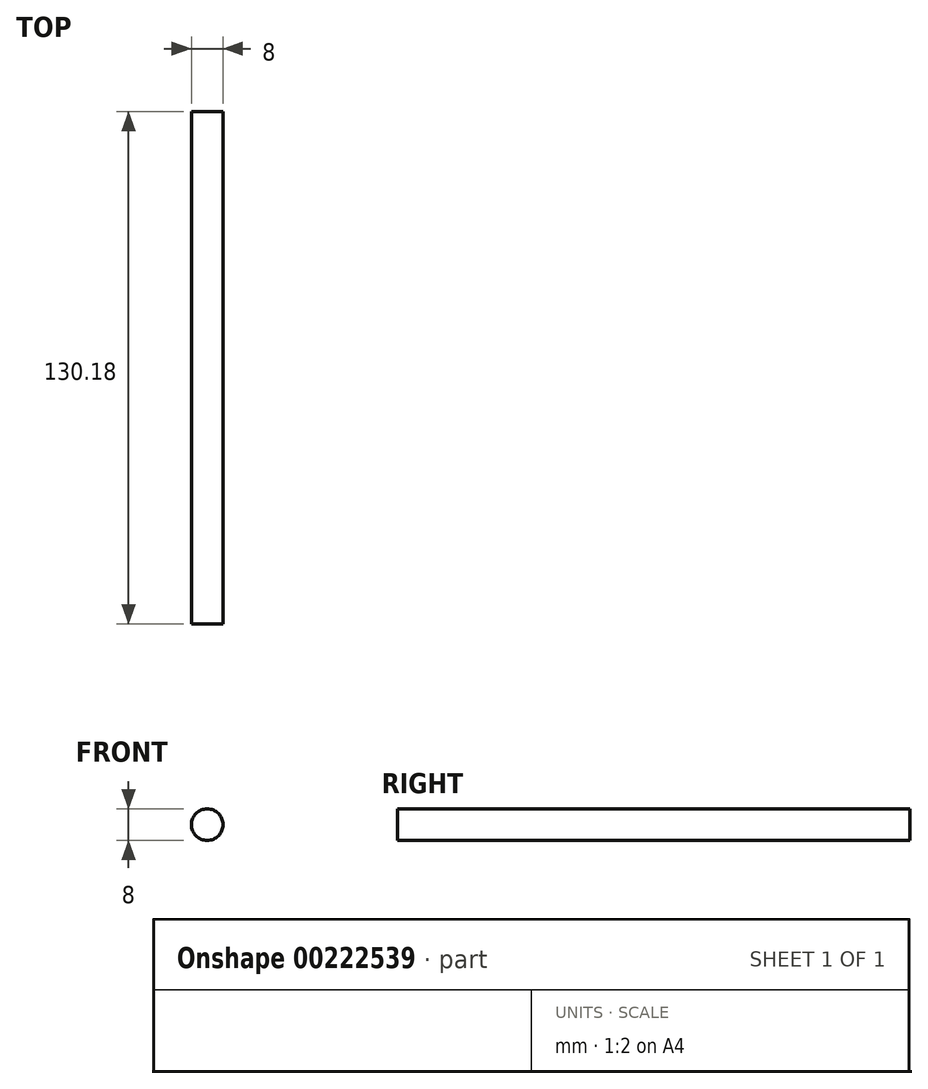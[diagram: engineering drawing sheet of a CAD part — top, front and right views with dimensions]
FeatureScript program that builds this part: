
annotation { "Feature Type Name" : "Feature", "Feature Type Description" : "" }
export const myFeature = defineFeature(function(context is Context, id is Id, definition is map)
    precondition{}
    {
        {
            var Q0;
            Q0=qCreatedBy(makeId("Front.planeOp"),FACE);
            var sketch = newSketch(context, id + "F0", { "sketchPlane" : qUnion([Q0])});
            skCircle(sketch, "E0", {"center": v(0, 0) * mm, "radius": 4 * mm});
            skSolve(sketch);
        }
        {
            var Q0;
            Q0 = qSketchRegion(id + "F0", true);
            extrude(context, id + "F1", {"entities" : qUnion([Q0]), "depth" : 130.17 * mm});
        }
    });
